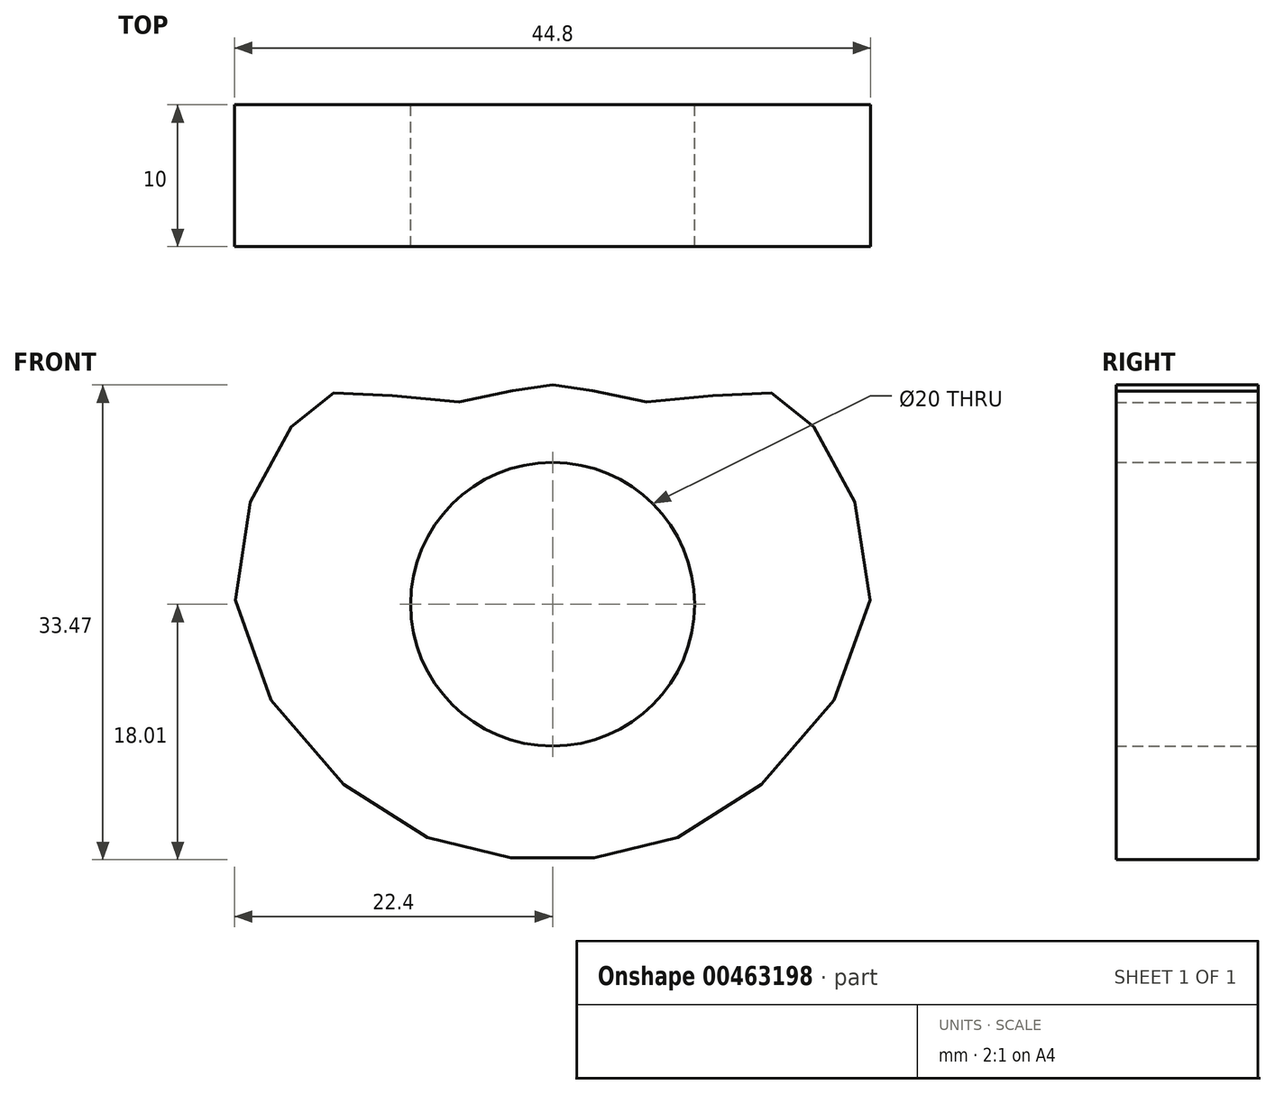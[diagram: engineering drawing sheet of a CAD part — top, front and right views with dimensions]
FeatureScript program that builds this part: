
annotation { "Feature Type Name" : "Feature", "Feature Type Description" : "" }
export const myFeature = defineFeature(function(context is Context, id is Id, definition is map)
    precondition{}
    {
        {
            var Q0;
            Q0=qCreatedBy(makeId("Front.planeOp"),FACE);
            var sketch = newSketch(context, id + "F0", { "sketchPlane" : qUnion([Q0])});
            skCircle(sketch, "E0", {"center": v(0, 0) * mm, "radius": 10 * mm});
            skPoint(sketch, "E1", {"position": v(-11.82, -14.85) * mm});
            skPoint(sketch, "E2", {"position": v(0, -18.01) * mm});
            skPoint(sketch, "E3", {"position": v(11.82, -14.85) * mm});
            skPoint(sketch, "E4", {"position": v(22.32, 0) * mm});
            skPoint(sketch, "E5", {"position": v(-22.32, 0) * mm});
            skPoint(sketch, "E6", {"position": v(-18.21, 12.76) * mm});
            skPoint(sketch, "E7", {"position": v(-14.49, 15.03) * mm});
            skPoint(sketch, "E8", {"position": v(-7.6, 14.22) * mm});
            skPoint(sketch, "E9", {"position": v(-2.58, 15.1) * mm});
            skPoint(sketch, "E10", {"position": v(0, 15.46) * mm});
            skPoint(sketch, "E11", {"position": v(2.58, 15.1) * mm});
            skPoint(sketch, "E12", {"position": v(7.6, 14.22) * mm});
            skPoint(sketch, "E13", {"position": v(14.49, 15.03) * mm});
            skPoint(sketch, "E14", {"position": v(18.21, 12.76) * mm});
            skFitSpline(sketch, "E15", {"points": [v(0, 15.46) * mm, v(-2.58, 15.1) * mm, v(-7.6, 14.22) * mm, v(-14.49, 15.03) * mm, v(-18.21, 12.76) * mm, v(-22.32, 0) * mm, v(-11.82, -14.85) * mm, v(0, -18.01) * mm, v(11.82, -14.85) * mm, v(22.32, 0) * mm, v(18.21, 12.76) * mm, v(14.49, 15.03) * mm, v(7.6, 14.22) * mm, v(2.58, 15.1) * mm, v(0, 15.46) * mm]});
            skSolve(sketch);
        }
        {
            var Q0;
            Q0=makeQuery(id+"F0.imprint","IMPRINT",FACE,{"disambiguationData":[TD([[makeQuery(id+"F0.imprint","IMPRINT",EDGE,{"derivedFrom":sQuery(id+"F0.wireOp",EDGE,"E0")}),-1.0]])]});
            extrude(context, id + "F1", {"entities" : qUnion([Q0]), "endBound" : BoundingType.SYMMETRIC, "depth" : 10 * mm});
        }
    });
